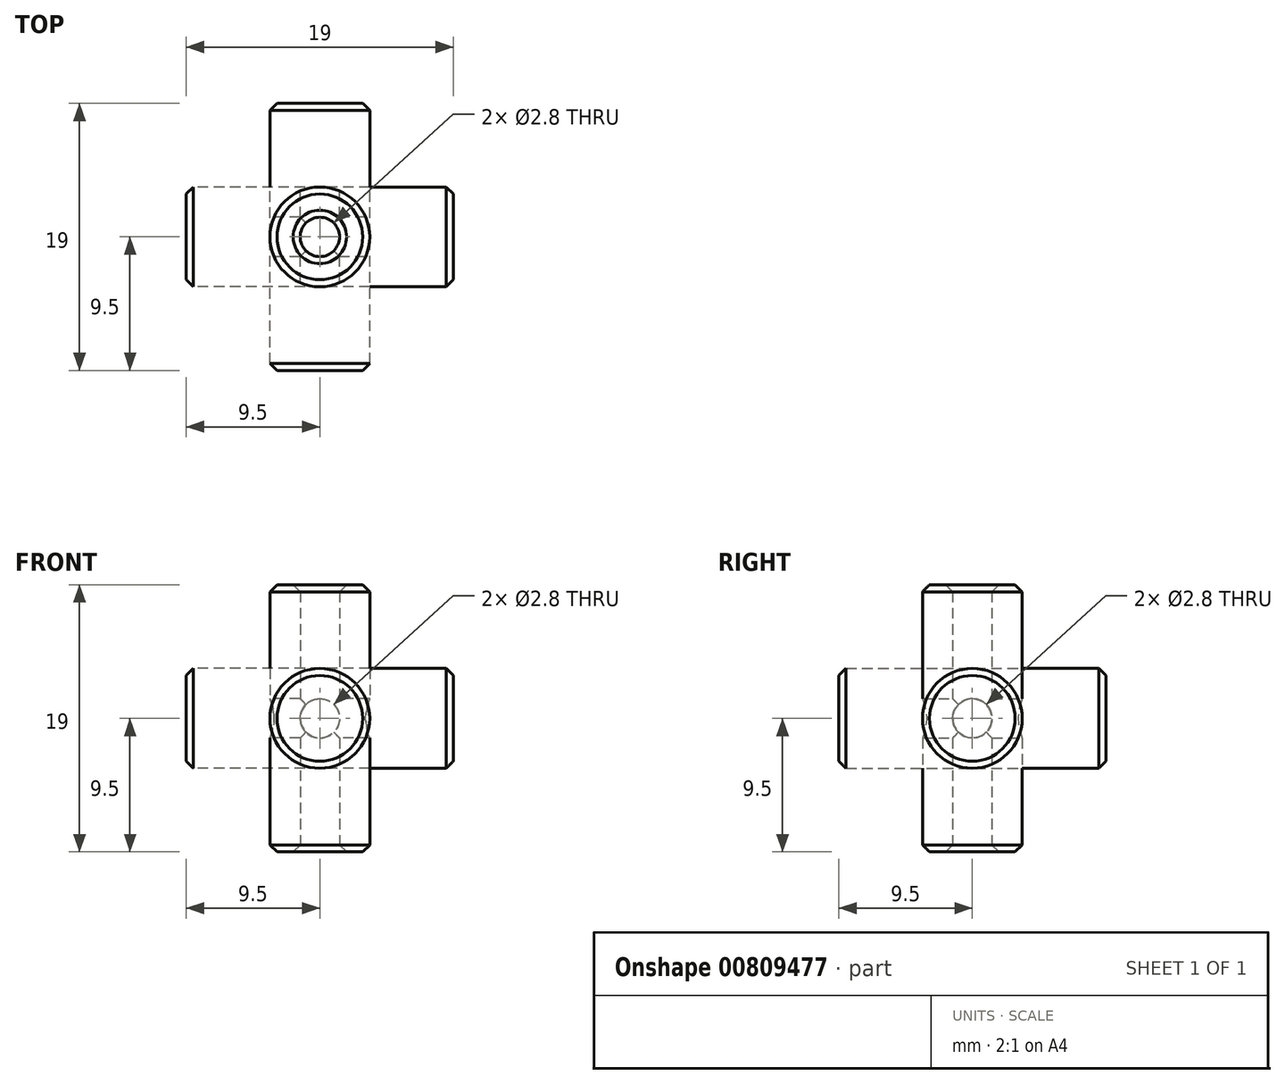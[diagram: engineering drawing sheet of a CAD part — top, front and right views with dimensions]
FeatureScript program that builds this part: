
annotation { "Feature Type Name" : "Feature", "Feature Type Description" : "" }
export const myFeature = defineFeature(function(context is Context, id is Id, definition is map)
    precondition{}
    {
        {
            var Q0;
            Q0=qCreatedBy(makeId("Front.planeOp"),FACE);
            var sketch = newSketch(context, id + "F0", { "sketchPlane" : qUnion([Q0])});
            skCircle(sketch, "E0", {"center": v(0, 0) * mm, "radius": 3.55 * mm});
            skSolve(sketch);
        }
        {
            var Q0;
            Q0=makeQuery(id+"F0.imprint","IMPRINT",FACE,{"disambiguationData":[TD([[makeQuery(id+"F0.imprint","IMPRINT",EDGE,{"derivedFrom":sQuery(id+"F0.wireOp",EDGE,"E0")}),1.0]])]});
            extrude(context, id + "F1", {"entities" : qUnion([Q0]), "endBound" : BoundingType.SYMMETRIC, "depth" : 19 * mm, "offsetDistance" : 25 * mm});
        }
        {
            var Q0;
            Q0=qCreatedBy(makeId("Front.planeOp"),FACE);
            var sketch = newSketch(context, id + "F2", { "sketchPlane" : qUnion([Q0])});
            skCircle(sketch, "E1", {"center": v(0, 0) * mm, "radius": 1.4 * mm});
            skSolve(sketch);
        }
        {
            var Q0;
            Q0 = qSketchRegion(id + "F2", true);
            extrude(context, id + "F3", {"entities" : qUnion([Q0]), "endBound" : BoundingType.SYMMETRIC, "depth" : 20 * mm, "offsetDistance" : 25 * mm});
        }
        {
            var Q0;
            Q0=qCreatedBy(makeId("Front.planeOp"),FACE);
            var sketch = newSketch(context, id + "F4", { "sketchPlane" : qUnion([Q0])});
            skLineSegment(sketch, "E2.bottom", {"start": v(0, 0) * mm, "end": v(10, 0) * mm});
            skLineSegment(sketch, "E2.top", {"start": v(0, 10) * mm, "end": v(10, 10) * mm});
            skLineSegment(sketch, "E2.left", {"start": v(0, 0) * mm, "end": v(0, 10) * mm});
            skLineSegment(sketch, "E2.right", {"start": v(10, 0) * mm, "end": v(10, 10) * mm});
            skSolve(sketch);
        }
        {
            var Q0;
            Q0 = qSketchRegion(id + "F4", true);
            extrude(context, id + "F5", {"entities" : qUnion([Q0]), "depth" : 10 * mm, "offsetDistance" : 25 * mm});
        }
        {
            var Q0;
            Q0=qCreatedBy(makeId("Origin.pointOp"),VERTEX);
            var Q1;
            Q1=makeQuery(id+"F5.opExtrude","CAP_VERTEX",VERTEX,{"disambiguationData":[OSD([sQuery(id+"F4.wireOp",EDGE,"E2.top"),sQuery(id+"F4.wireOp",EDGE,"E2.right")])],"isStart":false});
            var Q2;
            Q2=makeQuery(id+"F5.opExtrude","CAP_VERTEX",VERTEX,{"disambiguationData":[OSD([sQuery(id+"F4.wireOp",EDGE,"E2.bottom"),sQuery(id+"F4.wireOp",EDGE,"E2.right")])],"isStart":false});
            cPlane(context, id + "F6", {"entities" : qUnion([Q0, Q1, Q2]), "cplaneType" : CPlaneType.THREE_POINT, "offset" : 25 * mm, "width" : 150 * mm, "height" : 150 * mm});
        }
        {
            var Q0;
            Q0=qCreatedBy(id+"F6.planeOp",FACE);
            var sketch = newSketch(context, id + "F7", { "sketchPlane" : qUnion([Q0])});
            skLineSegment(sketch, "E3", {"start": v(0, 0) * mm, "end": v(14.14, 10) * mm});
            skSolve(sketch);
        }
        {
            var Q0;
            Q0=makeQuery(id+"F5.opExtrude","SWEPT_BODY",BODY,{"disambiguationData":[OSD([sQuery(id+"F4.wireOp",EDGE,"E2.bottom"),sQuery(id+"F4.wireOp",EDGE,"E2.top"),sQuery(id+"F4.wireOp",EDGE,"E2.left"),sQuery(id+"F4.wireOp",EDGE,"E2.right")])]});
            deleteBodies(context, id + "F8", {"entities" : qUnion([Q0])});
        }
        {
            var Q0;
            Q0=makeQuery(id+"F3.opExtrude","SWEPT_BODY",BODY,{"disambiguationData":[OSD([sQuery(id+"F2.wireOp",EDGE,"E1")])]});
            var Q1;
            Q1=makeQuery(id+"F1.opExtrude","SWEPT_BODY",BODY,{"disambiguationData":[OSD([sQuery(id+"F0.wireOp",EDGE,"E0")])]});
            var Q2;
            Q2=sQuery(id+"F7.wireOp",EDGE,"E3");
            circularPattern(context, id + "F9", {"entities" : qUnion([Q0, Q1]), "axis" : qUnion([Q2]), "angle" : 360 * degree, "instanceCount" : 3, "equalSpace" : true});
        }
        {
            var Q0;
            Q0=makeQuery(id+"F9.opPattern","COPY",BODY,{"derivedFrom":makeQuery(id+"F3.opExtrude","SWEPT_BODY",BODY,{"disambiguationData":[OSD([sQuery(id+"F2.wireOp",EDGE,"E1")])]}),"instanceName":"2"});
            var Q1;
            Q1=makeQuery(id+"F9.opPattern","COPY",BODY,{"derivedFrom":makeQuery(id+"F3.opExtrude","SWEPT_BODY",BODY,{"disambiguationData":[OSD([sQuery(id+"F2.wireOp",EDGE,"E1")])]}),"instanceName":"1"});
            var Q2;
            Q2=makeQuery(id+"F3.opExtrude","SWEPT_BODY",BODY,{"disambiguationData":[OSD([sQuery(id+"F2.wireOp",EDGE,"E1")])]});
            var Q3;
            Q3=makeQuery(id+"F9.opPattern","COPY",BODY,{"derivedFrom":makeQuery(id+"F1.opExtrude","SWEPT_BODY",BODY,{"disambiguationData":[OSD([sQuery(id+"F0.wireOp",EDGE,"E0")])]}),"instanceName":"2"});
            booleanBodies(context, id + "F10", {"operationType" : BooleanOperationType.SUBTRACTION, "tools" : qUnion([Q0, Q1, Q2]), "targets" : qUnion([Q3])});
        }
        {
            var Q0;
            Q0=makeQuery(id+"F9.opPattern","COPY",FACE,{"derivedFrom":makeQuery(id+"F1.opExtrude","CAP_FACE",FACE,{"disambiguationData":[OSD([sQuery(id+"F0.wireOp",EDGE,"E0")])],"isStart":false}),"instanceName":"2"});
            var Q1;
            Q1=makeQuery(id+"F1.opExtrude","CAP_FACE",FACE,{"disambiguationData":[OSD([sQuery(id+"F0.wireOp",EDGE,"E0")])],"isStart":false});
            var Q2;
            Q2=makeQuery(id+"F9.opPattern","COPY",FACE,{"derivedFrom":makeQuery(id+"F1.opExtrude","CAP_FACE",FACE,{"disambiguationData":[OSD([sQuery(id+"F0.wireOp",EDGE,"E0")])],"isStart":false}),"instanceName":"1"});
            var Q3;
            Q3=makeQuery(id+"F1.opExtrude","CAP_FACE",FACE,{"disambiguationData":[OSD([sQuery(id+"F0.wireOp",EDGE,"E0")])],"isStart":true});
            var Q4;
            Q4=makeQuery(id+"F9.opPattern","COPY",FACE,{"derivedFrom":makeQuery(id+"F1.opExtrude","CAP_FACE",FACE,{"disambiguationData":[OSD([sQuery(id+"F0.wireOp",EDGE,"E0")])],"isStart":true}),"instanceName":"1"});
            var Q5;
            Q5=makeQuery(id+"F9.opPattern","COPY",FACE,{"derivedFrom":makeQuery(id+"F1.opExtrude","CAP_FACE",FACE,{"disambiguationData":[OSD([sQuery(id+"F0.wireOp",EDGE,"E0")])],"isStart":true}),"instanceName":"2"});
            chamfer(context, id + "F11", {"entities" : qUnion([Q0, Q1, Q2, Q3, Q4, Q5]), "width" : 0.5 * mm, "tangentPropagation" : true});
        }
    });
